# Revit family: track lifgt
name_source: partatom
category: Lighting Fixtures
units: mm (PartAtom-declared; Revit-internal decimal feet)

## family parameters
Always vertical = No
Cut with Voids When Loaded = No
Light Source = Yes
Part Type = Normal
Room Calculation Point = No
Round Connector Dimension = Use Radius
Shared = No
Work Plane-Based = No

## types (1)
- std
    Apparent Load = 40 VA
    Apparent Power = 40 VA
    Application = Lighting
    Application Environment = Indoor
    Color Filter = 16777215
    Dimming Lamp Color Temperature Shift = <None>
    Emergency = No
    Emit Shape Visible in Rendering = No
    Emit from Circle Diameter = 610 mm
    IP Rating = IP20
    Lamp = LED
    Load Classification = Lighting
    Luminaire Type = Pendant
    Mounting Type = Multi-directional
    Number of Poles = 1
    Photometric Web File = generic
    Power Factor = 1
    Real Power = 40 W
    Tilt Angle = 60.00°
    Total Power = 40 W
    Voltage = 230 V
    W2D = 60 mm  [stored 0.19685 ft]

note: [stored X ft] marks values corroborated as IEEE doubles in the binary element streams (Revit-internal decimal feet)

## geometry (parser evidence)
native form markers: Sweep x14
no freeform markers — native parametric forms only
